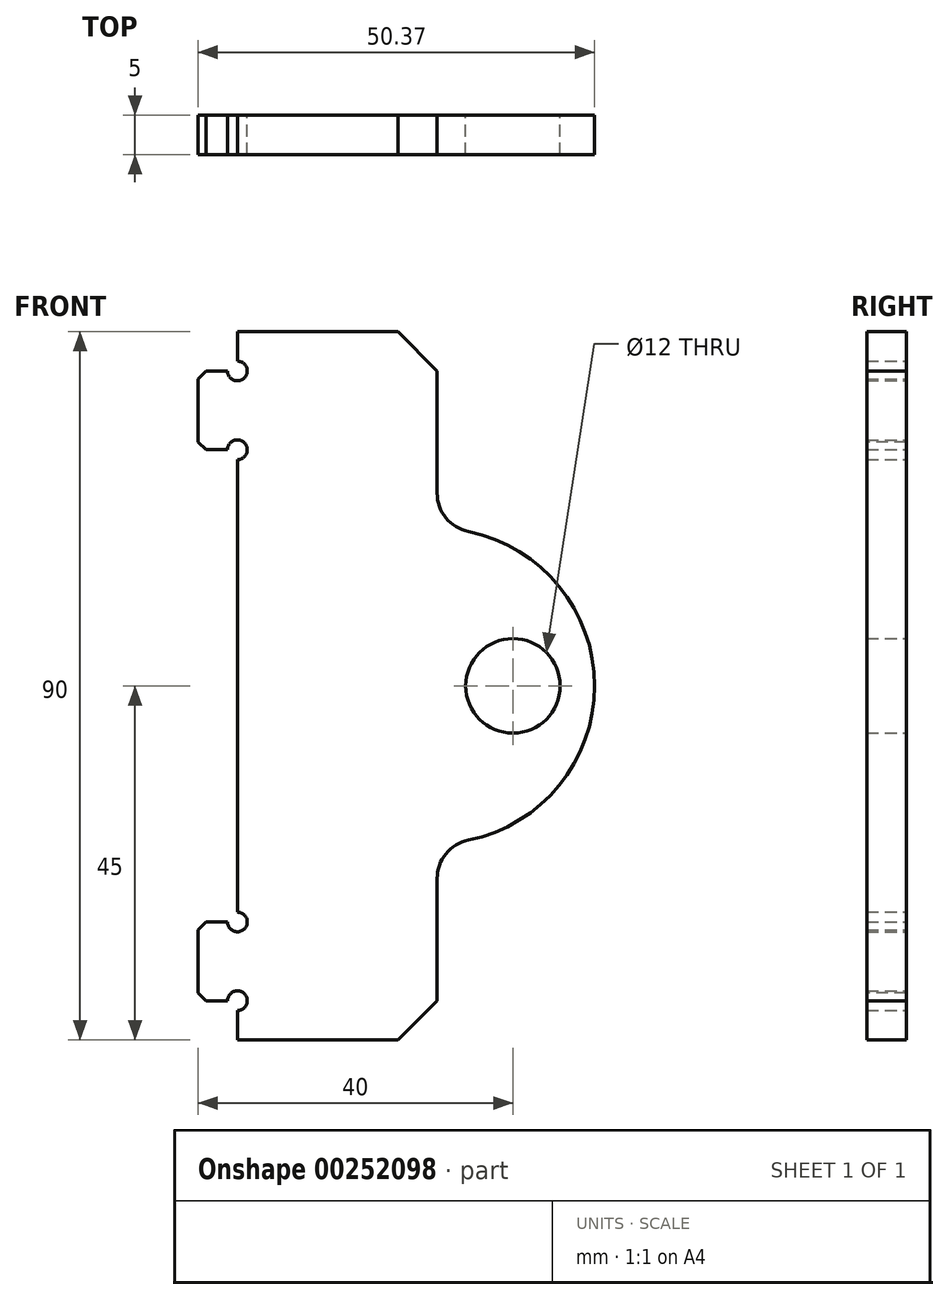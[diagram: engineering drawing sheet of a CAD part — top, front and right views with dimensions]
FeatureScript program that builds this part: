
annotation { "Feature Type Name" : "Feature", "Feature Type Description" : "" }
export const myFeature = defineFeature(function(context is Context, id is Id, definition is map)
    precondition{}
    {
        {
            var Q0;
            Q0=qCreatedBy(makeId("Front.planeOp"),FACE);
            var sketch = newSketch(context, id + "F0", { "sketchPlane" : qUnion([Q0])});
            skLineSegment(sketch, "E0.bottom", {"start": v(5, 30) * mm, "end": v(-5, 30) * mm});
            skLineSegment(sketch, "E0.top", {"start": v(5, 40) * mm, "end": v(-5, 40) * mm});
            skLineSegment(sketch, "E0.left", {"start": v(5, 30) * mm, "end": v(5, 40) * mm});
            skLineSegment(sketch, "E0.right", {"start": v(-5, 30) * mm, "end": v(-5, 40) * mm});
            skPoint(sketch, "E0.middle", {"position": v(0, 35) * mm});
            skLineSegment(sketch, "E1.MirrorCS", {"start": v(5, -30) * mm, "end": v(-5, -30) * mm});
            skPoint(sketch, "E2.MirrorP", {"position": v(0, -35) * mm});
            skLineSegment(sketch, "E3.MirrorCS", {"start": v(-5, -30) * mm, "end": v(-5, -40) * mm});
            skLineSegment(sketch, "E4.MirrorCS", {"start": v(5, -30) * mm, "end": v(5, -40) * mm});
            skLineSegment(sketch, "E5.MirrorCS", {"start": v(5, -40) * mm, "end": v(-5, -40) * mm});
            skLineSegment(sketch, "E6", {"start": v(0, 0) * mm, "end": v(0, 45) * mm});
            skLineSegment(sketch, "E7", {"start": v(0, 45) * mm, "end": v(25.37, 45) * mm});
            skLineSegment(sketch, "E8", {"start": v(25.37, 45) * mm, "end": v(25.37, 24.5) * mm});
            skLineSegment(sketch, "E9", {"start": v(5.37, 0) * mm, "end": v(0, 0) * mm});
            skLineSegment(sketch, "E10.MirrorCS", {"start": v(0, 0) * mm, "end": v(0, -45) * mm});
            skLineSegment(sketch, "E11.MirrorCS", {"start": v(0, -45) * mm, "end": v(25.37, -45) * mm});
            skLineSegment(sketch, "E12.MirrorCS", {"start": v(25.37, -45) * mm, "end": v(25.37, -24.5) * mm});
            skArc(sketch, "E13", {"start": v(29.37, -19.6) * mm, "mid": v(45.37, 0) * mm, "end": v(29.37, 19.6) * mm});
            skCircle(sketch, "E14", {"center": v(35, 0) * mm, "radius": 6 * mm});
            skPoint(sketch, "E15.visualSharp", {"position": v(25.37, 20) * mm});
            skArc(sketch, "E15.filletArc", {"start": v(25.37, 24.5) * mm, "mid": v(26.5, 21.33) * mm, "end": v(29.37, 19.6) * mm});
            skPoint(sketch, "E16.visualSharp", {"position": v(25.37, -20) * mm});
            skArc(sketch, "E16.filletArc", {"start": v(29.37, -19.6) * mm, "mid": v(26.5, -21.33) * mm, "end": v(25.37, -24.5) * mm});
            skCircle(sketch, "E17", {"center": v(0, 40) * mm, "radius": 1.25 * mm});
            skCircle(sketch, "E18", {"center": v(0, 30) * mm, "radius": 1.25 * mm});
            skCircle(sketch, "E19", {"center": v(0, -30) * mm, "radius": 1.25 * mm});
            skCircle(sketch, "E20", {"center": v(0, -40) * mm, "radius": 1.25 * mm});
            skSolve(sketch);
        }
        {
            var Q0;
            {var subQ14=sQuery(id+"F0.wireOp",EDGE,"E0.left");Q0=makeQuery(id+"F0.imprint","IMPRINT",FACE,{"disambiguationData":[TD([[makeQuery(id+"F0.imprint","IMPRINT",EDGE,{"derivedFrom":subQ14}),-1.0]])]});}
            var Q1;
            {var subQ8=sQuery(id+"F0.wireOp",EDGE,"E4.MirrorCS");Q1=makeQuery(id+"F0.imprint","IMPRINT",FACE,{"disambiguationData":[TD([[makeQuery(id+"F0.imprint","IMPRINT",EDGE,{"derivedFrom":subQ8}),-1.0]])]});}
            var Q2;
            {var subQ8=sQuery(id+"F0.wireOp",EDGE,"E3.MirrorCS");Q2=makeQuery(id+"F0.imprint","IMPRINT",FACE,{"disambiguationData":[TD([[makeQuery(id+"F0.imprint","IMPRINT",EDGE,{"derivedFrom":subQ8}),1.0]])]});}
            var Q3;
            {var subQ0=sQuery(id+"F0.wireOp",EDGE,"E0.left");Q3=makeQuery(id+"F0.imprint","IMPRINT",FACE,{"disambiguationData":[TD([[makeQuery(id+"F0.imprint","IMPRINT",EDGE,{"derivedFrom":subQ0}),1.0]])]});}
            var Q4;
            {var subQ0=sQuery(id+"F0.wireOp",EDGE,"E0.right");Q4=makeQuery(id+"F0.imprint","IMPRINT",FACE,{"disambiguationData":[TD([[makeQuery(id+"F0.imprint","IMPRINT",EDGE,{"derivedFrom":subQ0}),-1.0]])]});}
            extrude(context, id + "F1", {"entities" : qUnion([Q0, Q1, Q2, Q3, Q4]), "endBound" : BoundingType.SYMMETRIC, "depth" : 5 * mm});
        }
        {
            var Q0;
            Q0=makeQuery(id+"F1.opExtrude","SWEPT_EDGE",EDGE,{"disambiguationData":[OSD([sQuery(id+"F0.wireOp",EDGE,"E7"),sQuery(id+"F0.wireOp",EDGE,"E8")])]});
            var Q1;
            Q1=makeQuery(id+"F1.opExtrude","SWEPT_EDGE",EDGE,{"disambiguationData":[OSD([sQuery(id+"F0.wireOp",EDGE,"E11.MirrorCS"),sQuery(id+"F0.wireOp",EDGE,"E12.MirrorCS")])]});
            chamfer(context, id + "F2", {"entities" : qUnion([Q0, Q1]), "width" : 5 * mm, "tangentPropagation" : true});
        }
        {
            var Q0;
            Q0=makeQuery(id+"F1.opExtrude","SWEPT_EDGE",EDGE,{"disambiguationData":[OSD([sQuery(id+"F0.wireOp",EDGE,"E0.top"),sQuery(id+"F0.wireOp",EDGE,"E0.right")])]});
            var Q1;
            Q1=makeQuery(id+"F1.opExtrude","SWEPT_EDGE",EDGE,{"disambiguationData":[OSD([sQuery(id+"F0.wireOp",EDGE,"E1.MirrorCS"),sQuery(id+"F0.wireOp",EDGE,"E3.MirrorCS")])]});
            var Q2;
            Q2=makeQuery(id+"F1.opExtrude","SWEPT_EDGE",EDGE,{"disambiguationData":[OSD([sQuery(id+"F0.wireOp",EDGE,"E0.bottom"),sQuery(id+"F0.wireOp",EDGE,"E0.right")])]});
            var Q3;
            Q3=makeQuery(id+"F1.opExtrude","SWEPT_EDGE",EDGE,{"disambiguationData":[OSD([sQuery(id+"F0.wireOp",EDGE,"E3.MirrorCS"),sQuery(id+"F0.wireOp",EDGE,"E5.MirrorCS")])]});
            chamfer(context, id + "F3", {"entities" : qUnion([Q0, Q1, Q2, Q3]), "width" : 1 * mm, "tangentPropagation" : true});
        }
    });
